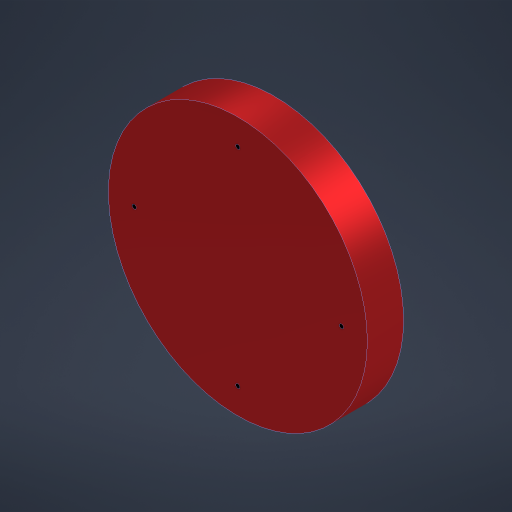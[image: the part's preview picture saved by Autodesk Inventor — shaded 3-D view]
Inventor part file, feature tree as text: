
AUTODESK INVENTOR PART (.ipt)
format: ipt  version: 2023 (Build 270158000, 158)  size: 237,568 bytes
history: native  units: mm
features: extrude x5, sketch x4, fillet x1, direct_edit x1, other x1
ambient origin geometry x8: Origin, YZ Plane, XZ Plane, XY Plane, X Axis, Y Axis, Z Axis, Center Point
bodies: Solid1 (feature_tree)
feature tree (12):
  extrude  "Extrusion1"  Depth=200.0mm
  fillet  "Fillet1"  Radius=30.0mm
  extrude  "Extrusion2"  Depth=30.0mm
  sketch  "Sketch11"  dims[d5=30.0mm d6=30.0mm]
  extrude  "Extrusion10"  Depth=30.0mm
  extrude  "Extrusion11"  Depth=10.0mm
  direct_edit  "Direct Edit3"
  extrude  "Extrusion12"  Depth=10.0mm
  sketch  "Sketch1"  dims[d0=200.0mm d1=200.0mm d2=30.0mm]
  sketch  "Sketch2"  dims[d3=30.0mm d4=30.0mm]
  sketch  "Sketch13"  dims[d7=30.0mm d8=30.0mm d9=30.0mm d10=10.0mm d11=0.0mm d12=10.0mm d13=125.0mm d14=7.5mm d15=0.0mm d145=200.0mm d146=0.0mm d147=200.0mm d148=0.0mm d149=15.0mm d150=10.0mm d151=10.0mm d153=3.0mm d154=3.0mm d155=3.0mm d156=3.0mm d157=200.0mm d158=0.0mm d64=0.5mm d65=0.872665mm d66=0.5mm d67=0.872665mm]
  other  "Scale3"
